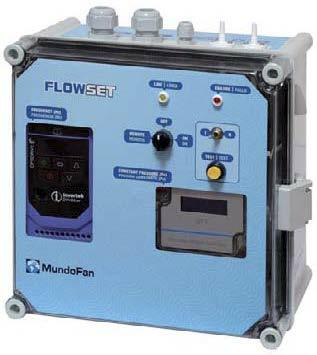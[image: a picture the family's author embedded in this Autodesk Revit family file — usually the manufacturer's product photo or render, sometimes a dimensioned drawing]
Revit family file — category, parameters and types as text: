
# Revit family: FLOWSET-11_VE10841
name_source: partatom
category: Aparatos eléctricos
revit_build: Autodesk Revit 2016 (Build: 20150220_1215(x64)
units: mm (PartAtom-declared; Revit-internal decimal feet)

## family parameters
Compartido = No
Corte con vacíos al cargar = No
Cota de conector redondo = Diámetro de uso
Mantener orientación de anotación = No
Número OmniClass = 23.80.00.00
Punto de cálculo de habitación = No
Se basa en plano de trabajo = No
Siempre vertical = Sí
Tipo de pieza = Caja de conexiones
Título OmniClass = Electric Power and Lighting

## types (1)
- FLOWSET
    Alimentación = 230Vac monofásico
    Corriente = 10,5 A
    Costo = 0 $
    Código de montaje = VE10841
    Descripción = CONTROL EFICIENCIA ENERGETICA PARA VENTILADORES - Caudal aire constante
    Dimensiones máx. = 270x300x170 mm
    Fabricante = SALVADOR ESCODA
    Imagen de tipo = flowset.jpg
    Leds = linea / fallo
    Modelo = FLOWSET 1,1kW
    Normativas = EN-ISO 14644-1:2000
    Potencia = 1,1 kW
    Regulación = Mediante sonda analógica de presión
    Salida = 230Vac monofásico
    Selector = 3 posiciones remoto / off / on
    URL = www.salvadorescoda.com
    Visualización = frecuencia (Hz) y presión (Pa)
